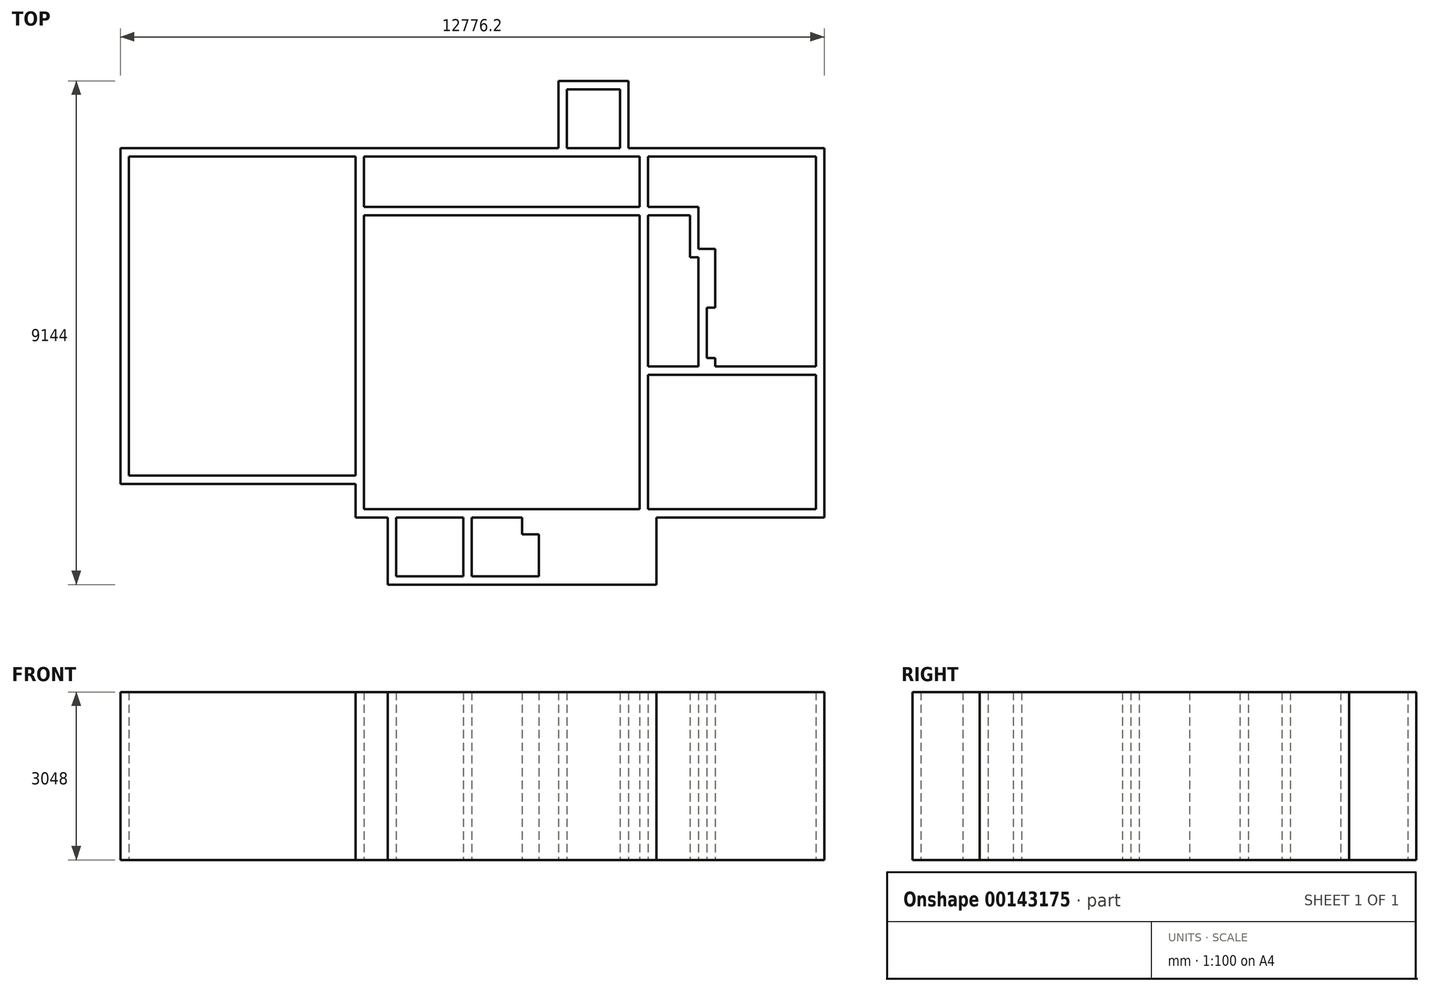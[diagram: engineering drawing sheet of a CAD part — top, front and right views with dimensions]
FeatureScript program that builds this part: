
annotation { "Feature Type Name" : "Feature", "Feature Type Description" : "" }
export const myFeature = defineFeature(function(context is Context, id is Id, definition is map)
    precondition{}
    {
        {
            var Q0;
            Q0=qCreatedBy(makeId("Top.planeOp"),FACE);
            var sketch = newSketch(context, id + "F0", { "sketchPlane" : qUnion([Q0])});
            skLineSegment(sketch, "E0.bottom", {"start": v(-8509, 6705.6) * mm, "end": v(-4826, 6705.6) * mm});
            skLineSegment(sketch, "E0.top", {"start": v(-8509, 0) * mm, "end": v(0, 0) * mm});
            skLineSegment(sketch, "E0.left", {"start": v(-8509, 6553.2) * mm, "end": v(-8509, 762) * mm});
            skLineSegment(sketch, "E0.right", {"start": v(0, 6705.6) * mm, "end": v(0, 0) * mm});
            skLineSegment(sketch, "E1.bottom", {"start": v(-7772.4, 0) * mm, "end": v(-6553.2, 0) * mm});
            skLineSegment(sketch, "E1.top", {"start": v(-7924.8, -1219.2) * mm, "end": v(-3048, -1219.2) * mm});
            skLineSegment(sketch, "E1.left", {"start": v(-7924.8, 0) * mm, "end": v(-7924.8, -1219.2) * mm});
            skLineSegment(sketch, "E1.right", {"start": v(-3048, 0) * mm, "end": v(-3048, -1219.2) * mm});
            skLineSegment(sketch, "E2.top", {"start": v(-3556, 7924.8) * mm, "end": v(-4826, 7924.8) * mm});
            skLineSegment(sketch, "E2.right", {"start": v(-4826, 6705.6) * mm, "end": v(-4826, 7924.8) * mm});
            skLineSegment(sketch, "E3.bottom", {"start": v(-8509, 6705.6) * mm, "end": v(-12776.2, 6705.6) * mm});
            skLineSegment(sketch, "E3.top", {"start": v(-8509, 609.6) * mm, "end": v(-12776.2, 609.6) * mm});
            skLineSegment(sketch, "E3.right", {"start": v(-12776.2, 6705.6) * mm, "end": v(-12776.2, 609.6) * mm});
            skLineSegment(sketch, "E4.bottom", {"start": v(-12623.8, 6553.2) * mm, "end": v(-8509, 6553.2) * mm});
            skLineSegment(sketch, "E4.top", {"start": v(-12623.8, 762) * mm, "end": v(-8509, 762) * mm});
            skLineSegment(sketch, "E4.left", {"start": v(-12623.8, 6553.2) * mm, "end": v(-12623.8, 762) * mm});
            skLineSegment(sketch, "E5.bottom", {"start": v(-8356.6, 6553.2) * mm, "end": v(-3352.8, 6553.2) * mm});
            skLineSegment(sketch, "E5.top", {"start": v(-8356.6, 5638.8) * mm, "end": v(-3352.8, 5638.8) * mm});
            skLineSegment(sketch, "E5.left", {"start": v(-8356.6, 6553.2) * mm, "end": v(-8356.6, 5638.8) * mm});
            skLineSegment(sketch, "E5.right", {"start": v(-3352.8, 6553.2) * mm, "end": v(-3352.8, 5638.8) * mm});
            skLineSegment(sketch, "E6.bottom", {"start": v(-8356.6, 5486.4) * mm, "end": v(-3352.8, 5486.4) * mm});
            skLineSegment(sketch, "E6.top", {"start": v(-8356.6, 152.4) * mm, "end": v(-3352.8, 152.4) * mm});
            skLineSegment(sketch, "E6.left", {"start": v(-8356.6, 5486.4) * mm, "end": v(-8356.6, 152.4) * mm});
            skLineSegment(sketch, "E6.right", {"start": v(-3352.8, 5486.4) * mm, "end": v(-3352.8, 152.4) * mm});
            skLineSegment(sketch, "E7.top", {"start": v(-7772.4, -1066.8) * mm, "end": v(-6553.2, -1066.8) * mm});
            skLineSegment(sketch, "E7.left", {"start": v(-7772.4, 0) * mm, "end": v(-7772.4, -1066.8) * mm});
            skLineSegment(sketch, "E7.right", {"start": v(-6553.2, 0) * mm, "end": v(-6553.2, -1066.8) * mm});
            skLineSegment(sketch, "E8.bottom", {"start": v(-3200.4, 2590.8) * mm, "end": v(-152.4, 2590.8) * mm});
            skLineSegment(sketch, "E8.top", {"start": v(-3200.4, 152.4) * mm, "end": v(-152.4, 152.4) * mm});
            skLineSegment(sketch, "E8.left", {"start": v(-3200.4, 2590.8) * mm, "end": v(-3200.4, 152.4) * mm});
            skLineSegment(sketch, "E8.right", {"start": v(-152.4, 2590.8) * mm, "end": v(-152.4, 152.4) * mm});
            skLineSegment(sketch, "E9.top", {"start": v(-4673.6, 7772.4) * mm, "end": v(-3708.4, 7772.4) * mm});
            skLineSegment(sketch, "E9.left", {"start": v(-4673.6, 6705.6) * mm, "end": v(-4673.6, 7772.4) * mm});
            skLineSegment(sketch, "E9.right", {"start": v(-3200.4, 152.4) * mm, "end": v(-3200.4, 2590.8) * mm});
            skLineSegment(sketch, "E10", {"start": v(-3200.4, 2743.2) * mm, "end": v(-3200.4, 5486.4) * mm});
            skLineSegment(sketch, "E11", {"start": v(-3200.4, 5486.4) * mm, "end": v(-2438.4, 5486.4) * mm});
            skLineSegment(sketch, "E12", {"start": v(-2438.4, 5486.4) * mm, "end": v(-2438.4, 4724.4) * mm});
            skLineSegment(sketch, "E13", {"start": v(-2438.4, 4724.4) * mm, "end": v(-2286, 4724.4) * mm});
            skLineSegment(sketch, "E14", {"start": v(-2286, 4724.4) * mm, "end": v(-2286, 2743.2) * mm});
            skLineSegment(sketch, "E15", {"start": v(-2286, 2743.2) * mm, "end": v(-3200.4, 2743.2) * mm});
            skLineSegment(sketch, "E16", {"start": v(-3200.4, 5638.8) * mm, "end": v(-3200.4, 6553.2) * mm});
            skLineSegment(sketch, "E17", {"start": v(-3200.4, 6553.2) * mm, "end": v(-152.4, 6553.2) * mm});
            skLineSegment(sketch, "E18", {"start": v(-152.4, 6553.2) * mm, "end": v(-152.4, 2743.2) * mm});
            skLineSegment(sketch, "E19", {"start": v(-152.4, 2743.2) * mm, "end": v(-1981.2, 2743.2) * mm});
            skLineSegment(sketch, "E20", {"start": v(-1981.2, 2743.2) * mm, "end": v(-1981.2, 2895.6) * mm});
            skLineSegment(sketch, "E21", {"start": v(-1981.2, 4876.8) * mm, "end": v(-2286, 4876.8) * mm});
            skLineSegment(sketch, "E22", {"start": v(-2286, 4876.8) * mm, "end": v(-2286, 5638.8) * mm});
            skLineSegment(sketch, "E23", {"start": v(-2286, 5638.8) * mm, "end": v(-3200.4, 5638.8) * mm});
            skLineSegment(sketch, "E24", {"start": v(-1981.2, 3810) * mm, "end": v(-2133.6, 3810) * mm});
            skLineSegment(sketch, "E25", {"start": v(-2133.6, 3810) * mm, "end": v(-2133.6, 2895.6) * mm});
            skLineSegment(sketch, "E26", {"start": v(-2133.6, 2895.6) * mm, "end": v(-1981.2, 2895.6) * mm});
            skLineSegment(sketch, "E27", {"start": v(-1981.2, 3810) * mm, "end": v(-1981.2, 4876.8) * mm});
            skLineSegment(sketch, "E28", {"start": v(-6400.8, 0) * mm, "end": v(-6400.8, -1066.8) * mm});
            skLineSegment(sketch, "E29", {"start": v(-6400.8, -1066.8) * mm, "end": v(-5181.6, -1066.8) * mm});
            skLineSegment(sketch, "E30", {"start": v(-5181.6, -1066.8) * mm, "end": v(-5181.6, -304.8) * mm});
            skLineSegment(sketch, "E31", {"start": v(-5181.6, -304.8) * mm, "end": v(-5486.4, -304.8) * mm});
            skLineSegment(sketch, "E32", {"start": v(-5486.4, -304.8) * mm, "end": v(-5486.4, 0) * mm});
            skLineSegment(sketch, "E33", {"start": v(-3556, 7924.8) * mm, "end": v(-3556, 6705.6) * mm});
            skLineSegment(sketch, "E34.trimOffspring", {"start": v(-8509, 609.6) * mm, "end": v(-8509, 0) * mm});
            skLineSegment(sketch, "E35.trimOffspring", {"start": v(-3708.4, 6705.6) * mm, "end": v(-3708.4, 7772.4) * mm});
            skLineSegment(sketch, "E36.trimOffspring", {"start": v(-4673.6, 6705.6) * mm, "end": v(-3708.4, 6705.6) * mm});
            skLineSegment(sketch, "E37.trimOffspring", {"start": v(-3556, 6705.6) * mm, "end": v(0, 6705.6) * mm});
            skLineSegment(sketch, "E38.trimOffspring", {"start": v(-6400.8, 0) * mm, "end": v(-5486.4, 0) * mm});
            skSolve(sketch);
        }
        {
            var Q0;
            Q0=makeQuery(id+"F0.imprint","IMPRINT",FACE,{"disambiguationData":[TD([[makeQuery(id+"F0.imprint","IMPRINT",EDGE,{"derivedFrom":sQuery(id+"F0.wireOp",EDGE,"E0.bottom")}),-1.0]])]});
            var Q1;
            Q1=makeQuery(id+"F0.imprint","IMPRINT",FACE,{"disambiguationData":[TD([[makeQuery(id+"F0.imprint","IMPRINT",EDGE,{"derivedFrom":sQuery(id+"F0.wireOp",EDGE,"E1.top")}),1.0]])]});
            extrude(context, id + "F1", {"entities" : qUnion([Q0, Q1]), "depth" : 3048 * mm});
        }
    });
